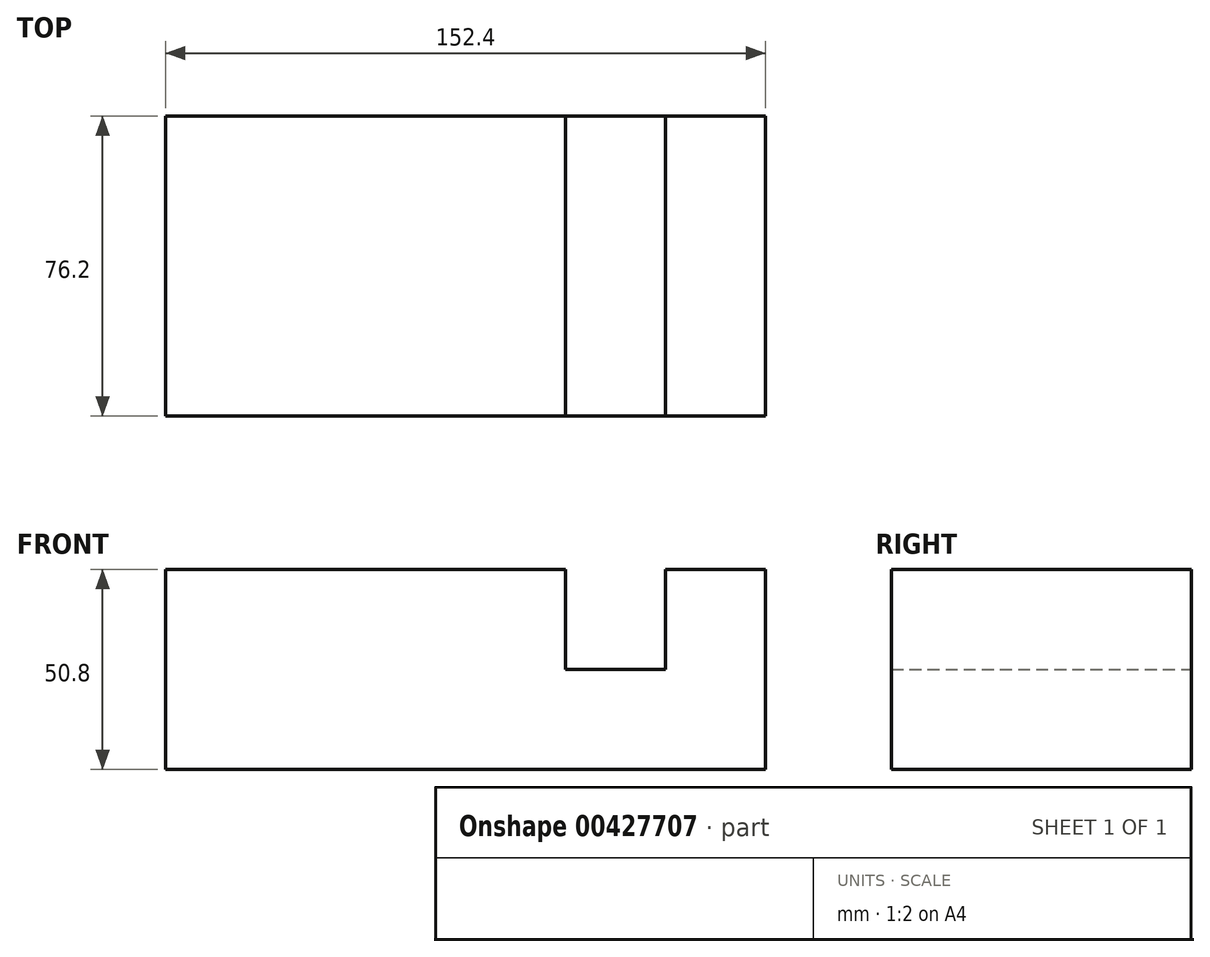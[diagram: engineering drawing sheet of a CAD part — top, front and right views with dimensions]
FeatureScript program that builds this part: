
annotation { "Feature Type Name" : "Feature", "Feature Type Description" : "" }
export const myFeature = defineFeature(function(context is Context, id is Id, definition is map)
    precondition{}
    {
        {
            var Q0;
            Q0=qCreatedBy(makeId("Front.planeOp"),FACE);
            var sketch = newSketch(context, id + "F0", { "sketchPlane" : qUnion([Q0])});
            skLineSegment(sketch, "E0", {"start": v(0, 0) * mm, "end": v(152.4, 0) * mm});
            skLineSegment(sketch, "E1", {"start": v(152.4, 0) * mm, "end": v(152.4, 50.8) * mm});
            skLineSegment(sketch, "E2", {"start": v(152.4, 50.8) * mm, "end": v(127, 50.8) * mm});
            skLineSegment(sketch, "E3", {"start": v(127, 50.8) * mm, "end": v(127, 25.4) * mm});
            skLineSegment(sketch, "E4", {"start": v(127, 25.4) * mm, "end": v(101.6, 25.4) * mm});
            skLineSegment(sketch, "E5", {"start": v(101.6, 25.4) * mm, "end": v(101.6, 50.8) * mm});
            skLineSegment(sketch, "E6", {"start": v(101.6, 50.8) * mm, "end": v(0, 50.8) * mm});
            skLineSegment(sketch, "E7", {"start": v(0, 50.8) * mm, "end": v(0, 0) * mm});
            skSolve(sketch);
        }
        {
            var Q0;
            Q0=makeQuery(id+"F0.imprint","IMPRINT",FACE,{"disambiguationData":[TD([[makeQuery(id+"F0.imprint","IMPRINT",EDGE,{"derivedFrom":sQuery(id+"F0.wireOp",EDGE,"E0")}),1.0]])]});
            extrude(context, id + "F1", {"entities" : qUnion([Q0]), "depth" : 76.2 * mm, "offsetDistance" : 25.4 * mm});
        }
    });
